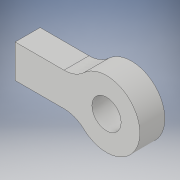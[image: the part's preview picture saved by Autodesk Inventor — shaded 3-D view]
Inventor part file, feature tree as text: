
AUTODESK INVENTOR PART (.ipt)
format: ipt  version: 2019 (Build 230136000, 136)  size: 109,056 bytes
history: native  units: mm
features: extrude x1, fillet x1, sketch x1
ambient origin geometry x8: Origin, YZ Plane, XZ Plane, XY Plane, X Axis, Y Axis, Z Axis, Center Point
bodies: Solid1 (feature_tree)
feature tree (3):
  extrude  "Extrusion1"  Depth=7.0mm
  fillet  "Fillet1"  Radius=8.0mm
  sketch  "Sketch1"  dims[d0=8.0mm d1=15.0mm d2=8.0mm d3=15.0mm d5=7.0mm d6=6.0mm d7=0.0mm d8=7.0mm]
